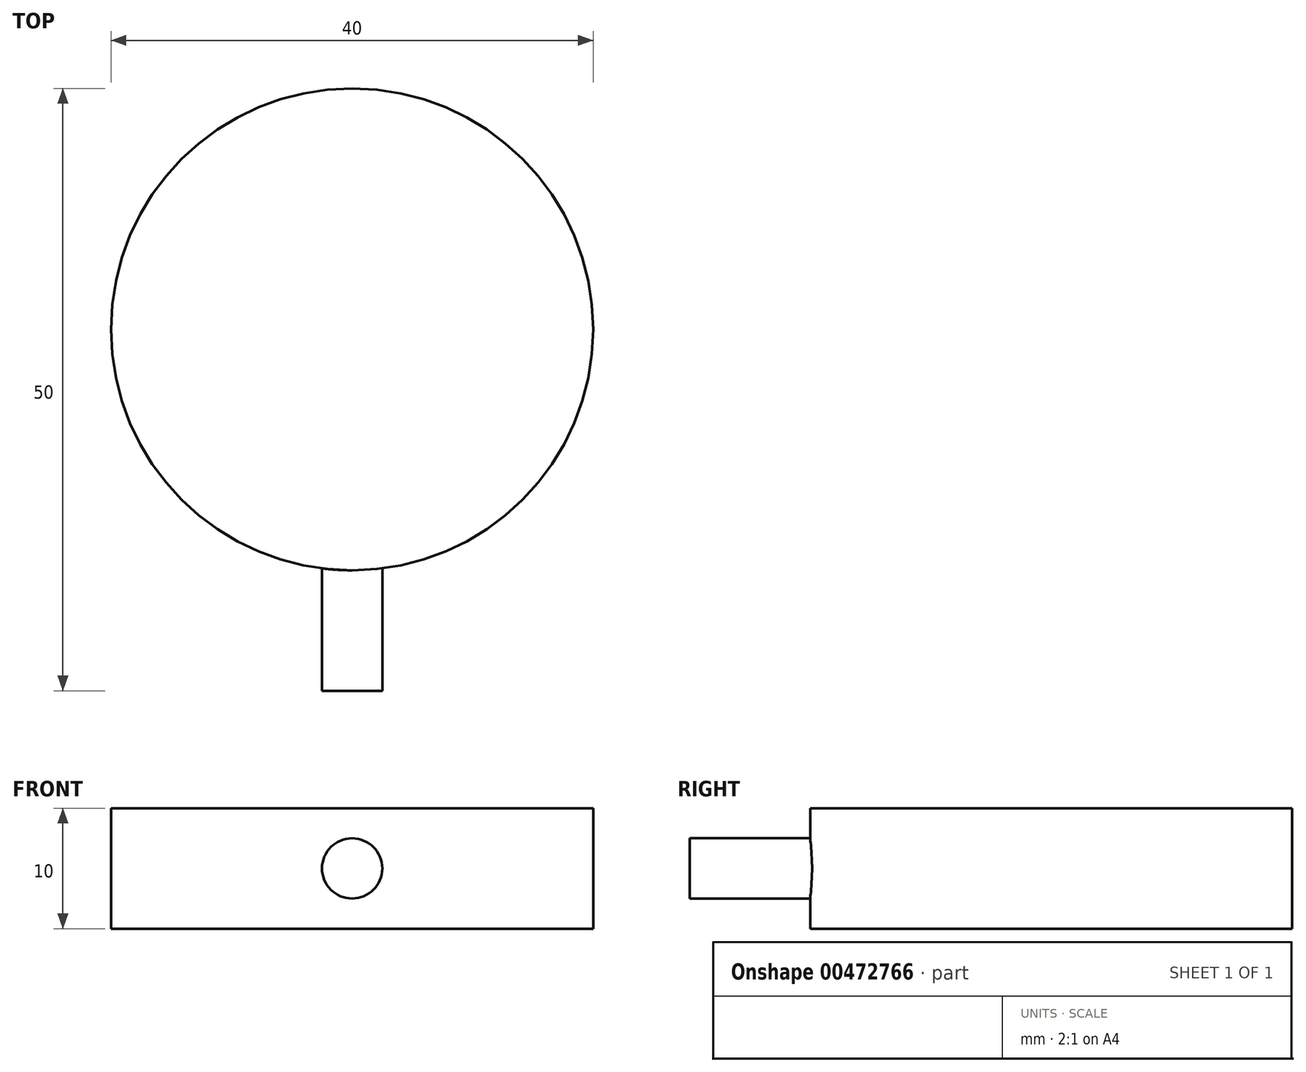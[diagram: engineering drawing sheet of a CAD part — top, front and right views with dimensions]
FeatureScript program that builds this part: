
annotation { "Feature Type Name" : "Feature", "Feature Type Description" : "" }
export const myFeature = defineFeature(function(context is Context, id is Id, definition is map)
    precondition{}
    {
        {
            assignVariable(context, id + "F0", {"name" : "lAe", "anyValue" : 10});
        }
        {
            assignVariable(context, id + "F1", {"name" : "dAe", "anyValue" : 40});
        }
        {
            var Q0;
            Q0=qCreatedBy(makeId("Top.planeOp"),FACE);
            var sketch = newSketch(context, id + "F2", { "sketchPlane" : qUnion([Q0])});
            skCircle(sketch, "E0", {"center": v(0, 0) * mm, "radius": 20 * mm});
            skSolve(sketch);
        }
        {
            var Q0;
            Q0 = qSketchRegion(id + "F2", true);
            extrude(context, id + "F3", {"entities" : qUnion([Q0]), "depth" : getVariable(context, 'lAe') * mm, "offsetDistance" : 25 * mm});
        }
        {
            var Q0;
            Q0=qCreatedBy(makeId("Front.planeOp"),FACE);
            var sketch = newSketch(context, id + "F4", { "sketchPlane" : qUnion([Q0])});
            skLineSegment(sketch, "E1", {"start": v(0, 0) * mm, "end": v(0, 10) * mm});
            skCircle(sketch, "E2", {"center": v(0, 5) * mm, "radius": 2.5 * mm});
            skSolve(sketch);
        }
        {
            var Q0;
            Q0 = qSketchRegion(id + "F4", true);
            extrude(context, id + "F5", {"entities" : qUnion([Q0]), "operationType" : NewBodyOperationType.ADD, "depth" : (getVariable(context, 'dAe') / 2 + 10) * mm, "offsetDistance" : 25 * mm});
        }
    });
